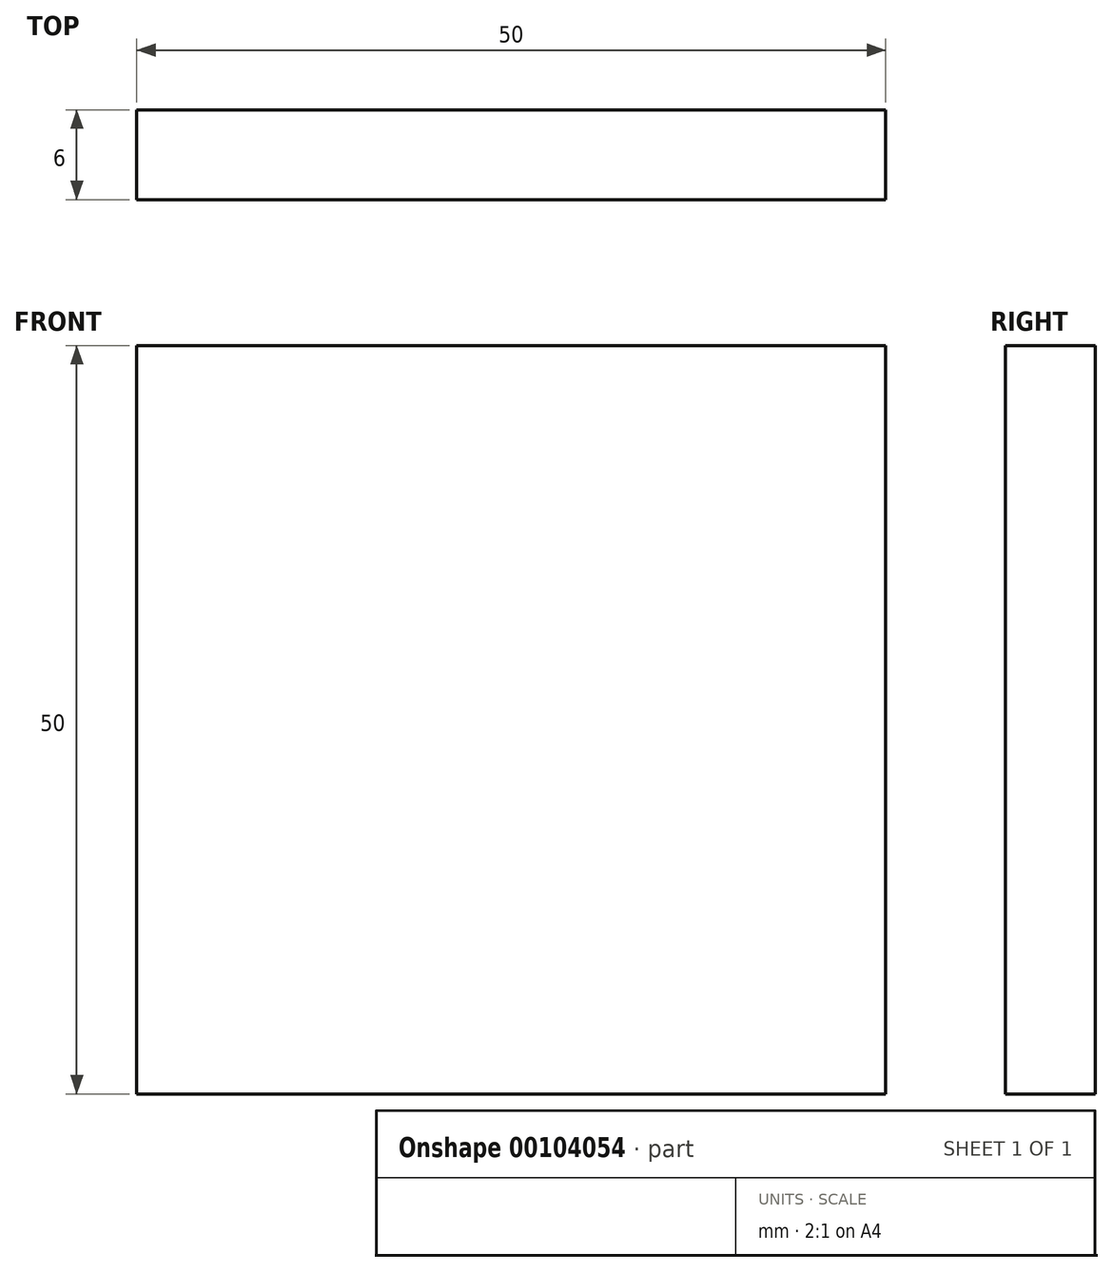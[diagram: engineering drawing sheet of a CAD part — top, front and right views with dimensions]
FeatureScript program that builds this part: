
annotation { "Feature Type Name" : "Feature", "Feature Type Description" : "" }
export const myFeature = defineFeature(function(context is Context, id is Id, definition is map)
    precondition{}
    {
        {
            var Q0;
            Q0=qCreatedBy(makeId("Front.planeOp"),FACE);
            var sketch = newSketch(context, id + "F0", { "sketchPlane" : qUnion([Q0])});
            skLineSegment(sketch, "E0.bottom", {"start": v(0, 0) * mm, "end": v(-50, 0) * mm});
            skLineSegment(sketch, "E0.top", {"start": v(0, 50) * mm, "end": v(-50, 50) * mm});
            skLineSegment(sketch, "E0.left", {"start": v(0, 0) * mm, "end": v(0, 50) * mm});
            skLineSegment(sketch, "E0.right", {"start": v(-50, 0) * mm, "end": v(-50, 50) * mm});
            skPoint(sketch, "E0.middle", {"position": v(-25, 25) * mm});
            skSolve(sketch);
        }
        {
            var Q0;
            Q0 = qSketchRegion(id + "F0", true);
            extrude(context, id + "F1", {"entities" : qUnion([Q0]), "depth" : 6 * mm});
        }
    });
